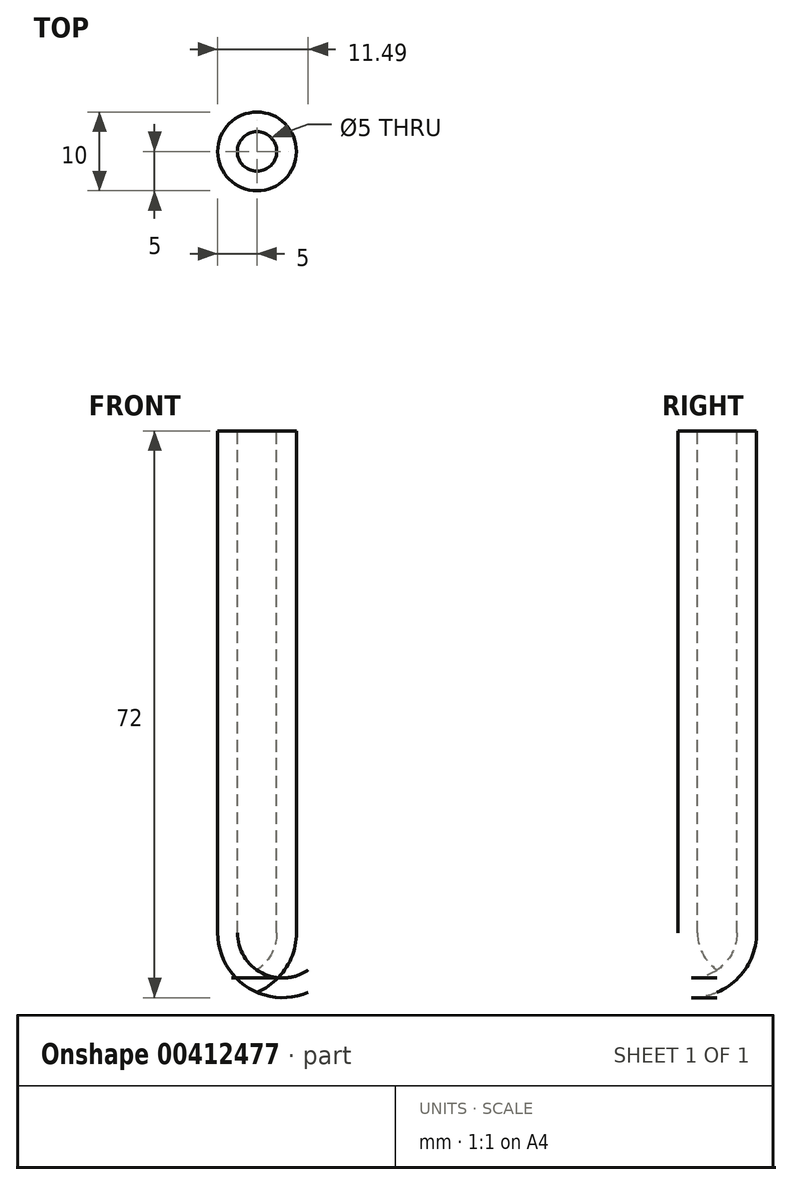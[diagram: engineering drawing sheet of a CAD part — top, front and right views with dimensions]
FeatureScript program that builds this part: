
annotation { "Feature Type Name" : "Feature", "Feature Type Description" : "" }
export const myFeature = defineFeature(function(context is Context, id is Id, definition is map)
    precondition{}
    {
        {
            var Q0;
            Q0=qCreatedBy(makeId("Front.planeOp"),FACE);
            var sketch = newSketch(context, id + "F0", { "sketchPlane" : qUnion([Q0])});
            skLineSegment(sketch, "E0", {"start": v(-3.25, 0) * mm, "end": v(-1, 0) * mm});
            skLineSegment(sketch, "E1", {"start": v(5, 8.25) * mm, "end": v(5, 72) * mm});
            skPoint(sketch, "E2.visualSharp", {"position": v(-6, 0) * mm});
            skPoint(sketch, "E3.visualSharp", {"position": v(5, 0) * mm});
            skArc(sketch, "E3.filletArc", {"start": v(-3.25, 0) * mm, "mid": v(2.58, 2.42) * mm, "end": v(5, 8.25) * mm});
            skLineSegment(sketch, "E4", {"start": v(0, 0) * mm, "end": v(0, 22) * mm, "construction": true});
            skLineSegment(sketch, "E5", {"start": v(5, 72) * mm, "end": v(0, 72) * mm});
            skLineSegment(sketch, "E6", {"start": v(0, 72) * mm, "end": v(0, 0) * mm});
            skSolve(sketch);
        }
        {
            var Q0;
            Q0 = qSketchRegion(id + "F0", true);
            var Q1;
            Q1=sQuery(id+"F0.wireOp",EDGE,"E6");
            revolve(context, id + "F1", {"entities" : qUnion([Q0]), "axis" : qUnion([Q1]), "revolveType" : RevolveType.FULL});
        }
        {
            var Q0;
            Q0=makeQuery(id+"F1.opRevolve","SWEPT_FACE",FACE,{"disambiguationData":[OSD([sQuery(id+"F0.wireOp",EDGE,"E5")])]});
            shell(context, id + "F2", {"entities" : qUnion([Q0]), "thickness" : 2.5 * mm});
        }
    });
